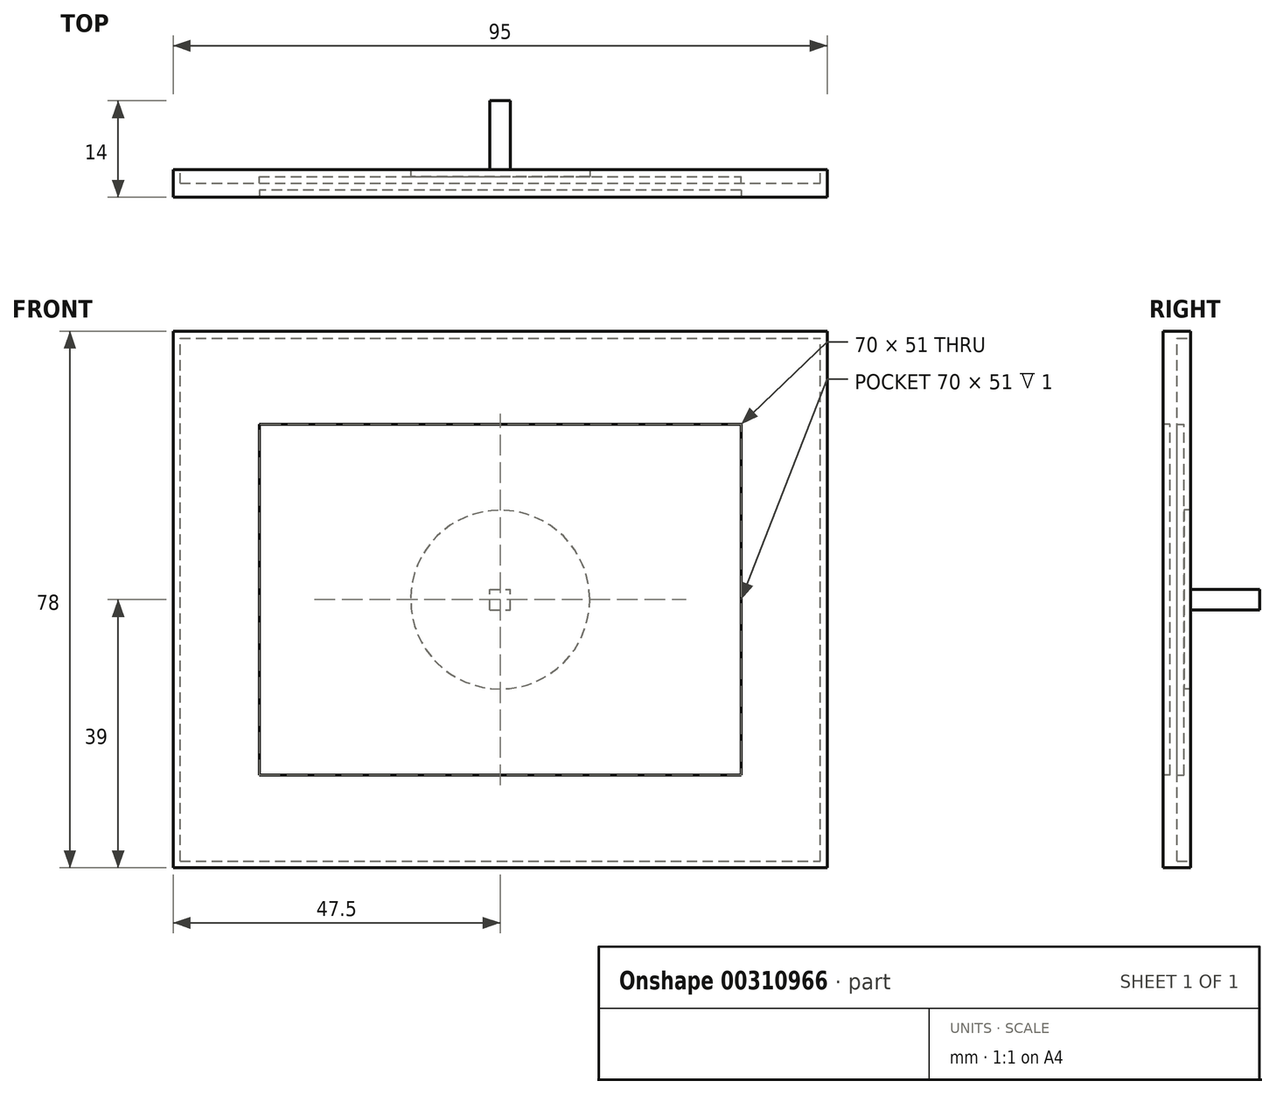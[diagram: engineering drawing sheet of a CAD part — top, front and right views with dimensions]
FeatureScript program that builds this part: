
annotation { "Feature Type Name" : "Feature", "Feature Type Description" : "" }
export const myFeature = defineFeature(function(context is Context, id is Id, definition is map)
    precondition{}
    {
        {
            var Q0;
            Q0=qCreatedBy(makeId("Front.planeOp"),FACE);
            var sketch = newSketch(context, id + "F0", { "sketchPlane" : qUnion([Q0])});
            skLineSegment(sketch, "E0.bottom", {"start": v(47.5, -39) * mm, "end": v(-47.5, -39) * mm});
            skLineSegment(sketch, "E0.top", {"start": v(47.5, 39) * mm, "end": v(-47.5, 39) * mm});
            skLineSegment(sketch, "E0.left", {"start": v(47.5, -39) * mm, "end": v(47.5, 39) * mm});
            skLineSegment(sketch, "E0.right", {"start": v(-47.5, -39) * mm, "end": v(-47.5, 39) * mm});
            skPoint(sketch, "E0.middle", {"position": v(0, 0) * mm});
            skSolve(sketch);
        }
        {
            var Q0;
            Q0=makeQuery(id+"F0.imprint","IMPRINT",FACE,{"disambiguationData":[TD([[makeQuery(id+"F0.imprint","IMPRINT",EDGE,{"derivedFrom":sQuery(id+"F0.wireOp",EDGE,"E0.bottom")}),-1.0]])]});
            extrude(context, id + "F1", {"entities" : qUnion([Q0]), "depth" : 4 * mm});
        }
        {
            var Q0;
            Q0=makeQuery(id+"F1.opExtrude","CAP_FACE",FACE,{"disambiguationData":[OSD([sQuery(id+"F0.wireOp",EDGE,"E0.bottom"),sQuery(id+"F0.wireOp",EDGE,"E0.top"),sQuery(id+"F0.wireOp",EDGE,"E0.left"),sQuery(id+"F0.wireOp",EDGE,"E0.right")])],"isStart":false});
            var sketch = newSketch(context, id + "F2", { "sketchPlane" : qUnion([Q0])});
            skLineSegment(sketch, "E1.bottom", {"start": v(35, -25.5) * mm, "end": v(-35, -25.5) * mm});
            skLineSegment(sketch, "E1.top", {"start": v(35, 25.5) * mm, "end": v(-35, 25.5) * mm});
            skLineSegment(sketch, "E1.left", {"start": v(35, -25.5) * mm, "end": v(35, 25.5) * mm});
            skLineSegment(sketch, "E1.right", {"start": v(-35, -25.5) * mm, "end": v(-35, 25.5) * mm});
            skPoint(sketch, "E1.middle", {"position": v(0, 0) * mm});
            skSolve(sketch);
        }
        {
            var Q0;
            Q0=makeQuery(id+"F2.imprint","IMPRINT",FACE,{"disambiguationData":[TD([[makeQuery(id+"F2.imprint","IMPRINT",EDGE,{"derivedFrom":sQuery(id+"F2.wireOp",EDGE,"E1.bottom")}),-1.0]])]});
            extrude(context, id + "F3", {"entities" : qUnion([Q0]), "operationType" : NewBodyOperationType.REMOVE, "oppositeDirection" : true, "depth" : 1 * mm});
        }
        {
            var Q0;
            Q0=makeQuery(id+"F1.opExtrude","CAP_FACE",FACE,{"disambiguationData":[OSD([sQuery(id+"F0.wireOp",EDGE,"E0.bottom"),sQuery(id+"F0.wireOp",EDGE,"E0.top"),sQuery(id+"F0.wireOp",EDGE,"E0.left"),sQuery(id+"F0.wireOp",EDGE,"E0.right")])],"isStart":true});
            var sketch = newSketch(context, id + "F4", { "sketchPlane" : qUnion([Q0])});
            skLineSegment(sketch, "E2.bottom", {"start": v(46.5, -38) * mm, "end": v(-46.5, -38) * mm});
            skLineSegment(sketch, "E2.top", {"start": v(46.5, 38) * mm, "end": v(-46.5, 38) * mm});
            skLineSegment(sketch, "E2.left", {"start": v(46.5, -38) * mm, "end": v(46.5, 38) * mm});
            skLineSegment(sketch, "E2.right", {"start": v(-46.5, -38) * mm, "end": v(-46.5, 38) * mm});
            skPoint(sketch, "E2.middle", {"position": v(0, 0) * mm});
            skLineSegment(sketch, "E3.bottom", {"start": v(35, -25.5) * mm, "end": v(-35, -25.5) * mm});
            skLineSegment(sketch, "E3.top", {"start": v(35, 25.5) * mm, "end": v(-35, 25.5) * mm});
            skLineSegment(sketch, "E3.left", {"start": v(35, -25.5) * mm, "end": v(35, 25.5) * mm});
            skLineSegment(sketch, "E3.right", {"start": v(-35, -25.5) * mm, "end": v(-35, 25.5) * mm});
            skSolve(sketch);
        }
        {
            var Q0;
            Q0=makeQuery(id+"F4.imprint","IMPRINT",FACE,{"disambiguationData":[TD([[makeQuery(id+"F4.imprint","IMPRINT",EDGE,{"derivedFrom":sQuery(id+"F4.wireOp",EDGE,"E2.bottom")}),-1.0]])]});
            extrude(context, id + "F5", {"entities" : qUnion([Q0]), "operationType" : NewBodyOperationType.REMOVE, "oppositeDirection" : true, "depth" : 2 * mm});
        }
        {
            var Q0;
            Q0=makeQuery(id+"F5.boolean.opBoolean","SPLIT",FACE,{"disambiguationData":[TD([makeQuery(id+"F5.opExtrude","SWEPT_FACE",FACE,{"disambiguationData":[OSD([sQuery(id+"F4.wireOp",EDGE,"E3.bottom")])]})])],"derivedFrom":makeQuery(id+"F1.opExtrude","CAP_FACE",FACE,{"disambiguationData":[OSD([sQuery(id+"F0.wireOp",EDGE,"E0.bottom"),sQuery(id+"F0.wireOp",EDGE,"E0.top"),sQuery(id+"F0.wireOp",EDGE,"E0.left"),sQuery(id+"F0.wireOp",EDGE,"E0.right")])],"isStart":true})});
            var sketch = newSketch(context, id + "F6", { "sketchPlane" : qUnion([Q0])});
            skLineSegment(sketch, "E4.bottom", {"start": v(35, -25.5) * mm, "end": v(-35, -25.5) * mm});
            skLineSegment(sketch, "E4.top", {"start": v(35, 25.5) * mm, "end": v(-35, 25.5) * mm});
            skLineSegment(sketch, "E4.left", {"start": v(35, -25.5) * mm, "end": v(35, 25.5) * mm});
            skLineSegment(sketch, "E4.right", {"start": v(-35, -25.5) * mm, "end": v(-35, 25.5) * mm});
            skPoint(sketch, "E4.middle", {"position": v(0, 0) * mm});
            skSolve(sketch);
        }
        {
            var Q0;
            Q0=makeQuery(id+"F6.imprint","IMPRINT",FACE,{"disambiguationData":[TD([[makeQuery(id+"F6.imprint","IMPRINT",EDGE,{"derivedFrom":sQuery(id+"F6.wireOp",EDGE,"E4.bottom")}),-1.0]])]});
            extrude(context, id + "F7", {"entities" : qUnion([Q0]), "operationType" : NewBodyOperationType.REMOVE, "oppositeDirection" : true, "depth" : 1 * mm});
        }
        {
            var Q0;
            Q0=makeQuery(id+"F7.boolean.opBoolean","COPY",FACE,{"derivedFrom":makeQuery(id+"F7.opExtrude","CAP_FACE",FACE,{"disambiguationData":[OSD([sQuery(id+"F6.wireOp",EDGE,"E4.bottom"),sQuery(id+"F6.wireOp",EDGE,"E4.top"),sQuery(id+"F6.wireOp",EDGE,"E4.left"),sQuery(id+"F6.wireOp",EDGE,"E4.right")])],"isStart":false})});
            var sketch = newSketch(context, id + "F8", { "sketchPlane" : qUnion([Q0])});
            skCircle(sketch, "E5", {"center": v(0, 0) * mm, "radius": 13 * mm});
            skSolve(sketch);
        }
        {
            var Q0;
            Q0=makeQuery(id+"F8.imprint","IMPRINT",FACE,{"disambiguationData":[TD([[makeQuery(id+"F8.imprint","IMPRINT",EDGE,{"derivedFrom":sQuery(id+"F8.wireOp",EDGE,"E5")}),1.0]])]});
            extrude(context, id + "F9", {"entities" : qUnion([Q0]), "operationType" : NewBodyOperationType.ADD, "depth" : 1 * mm});
        }
        {
            var Q0;
            Q0=makeQuery(id+"F9.opExtrude","CAP_FACE",FACE,{"disambiguationData":[OSD([sQuery(id+"F8.wireOp",EDGE,"E5")])],"isStart":false});
            var sketch = newSketch(context, id + "F10", { "sketchPlane" : qUnion([Q0])});
            skLineSegment(sketch, "E6.bottom", {"start": v(1.5, -1.5) * mm, "end": v(-1.5, -1.5) * mm});
            skLineSegment(sketch, "E6.top", {"start": v(1.5, 1.5) * mm, "end": v(-1.5, 1.5) * mm});
            skLineSegment(sketch, "E6.left", {"start": v(1.5, -1.5) * mm, "end": v(1.5, 1.5) * mm});
            skLineSegment(sketch, "E6.right", {"start": v(-1.5, -1.5) * mm, "end": v(-1.5, 1.5) * mm});
            skPoint(sketch, "E6.middle", {"position": v(0, 0) * mm});
            skSolve(sketch);
        }
        {
            var Q0;
            Q0=makeQuery(id+"F10.imprint","IMPRINT",FACE,{"disambiguationData":[TD([[makeQuery(id+"F10.imprint","IMPRINT",EDGE,{"derivedFrom":sQuery(id+"F10.wireOp",EDGE,"E6.bottom")}),-1.0]])]});
            extrude(context, id + "F11", {"entities" : qUnion([Q0]), "operationType" : NewBodyOperationType.ADD, "depth" : 10 * mm});
        }
    });
